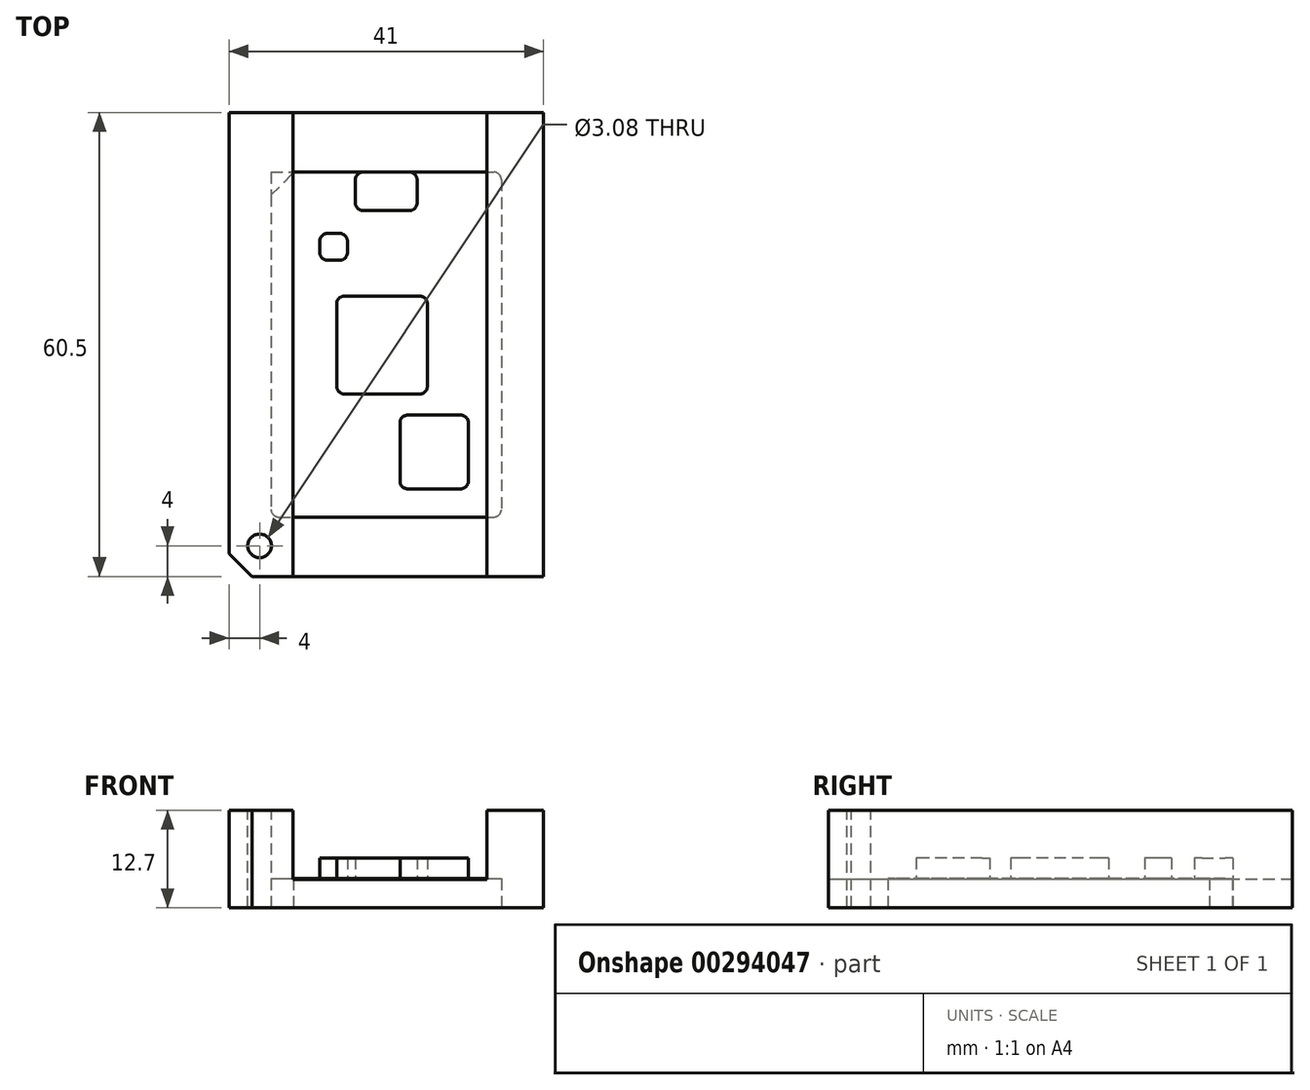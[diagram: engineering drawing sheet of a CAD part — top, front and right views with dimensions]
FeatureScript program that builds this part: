
annotation { "Feature Type Name" : "Feature", "Feature Type Description" : "" }
export const myFeature = defineFeature(function(context is Context, id is Id, definition is map)
    precondition{}
    {
        {
            var Q0;
            Q0=qCreatedBy(makeId("Top.planeOp"),FACE);
            var sketch = newSketch(context, id + "F0", { "sketchPlane" : qUnion([Q0])});
            skLineSegment(sketch, "E0.bottom", {"start": v(-20.5, -30.25) * mm, "end": v(20.5, -30.25) * mm});
            skLineSegment(sketch, "E0.top", {"start": v(-20.5, 30.25) * mm, "end": v(20.5, 30.25) * mm});
            skLineSegment(sketch, "E0.left", {"start": v(-20.5, -30.25) * mm, "end": v(-20.5, 30.25) * mm});
            skLineSegment(sketch, "E0.right", {"start": v(20.5, -30.25) * mm, "end": v(20.5, 30.25) * mm});
            skPoint(sketch, "E0.middle", {"position": v(0, 0) * mm});
            skSolve(sketch);
        }
        {
            var Q0;
            Q0 = qSketchRegion(id + "F0", true);
            extrude(context, id + "F1", {"entities" : qUnion([Q0]), "depth" : 12.7 * mm});
        }
        {
            var Q0;
            Q0=makeQuery(id+"F1.opExtrude","CAP_FACE",FACE,{"disambiguationData":[OSD([sQuery(id+"F0.wireOp",EDGE,"E0.bottom"),sQuery(id+"F0.wireOp",EDGE,"E0.top"),sQuery(id+"F0.wireOp",EDGE,"E0.left"),sQuery(id+"F0.wireOp",EDGE,"E0.right")])],"isStart":false});
            var sketch = newSketch(context, id + "F2", { "sketchPlane" : qUnion([Q0])});
            skLineSegment(sketch, "E1", {"start": v(-20.5, -27.25) * mm, "end": v(-17.5, -30.25) * mm});
            skLineSegment(sketch, "E2", {"start": v(-17.5, -30.25) * mm, "end": v(-20.5, -30.25) * mm});
            skLineSegment(sketch, "E3", {"start": v(-20.5, -30.25) * mm, "end": v(-20.5, -27.25) * mm});
            skCircle(sketch, "E4", {"center": v(-16.5, -26.25) * mm, "radius": 1.54 * mm});
            skLineSegment(sketch, "E5", {"start": v(-20.5, -30.25) * mm, "end": v(-20.5, -26.25) * mm, "construction": true});
            skLineSegment(sketch, "E6", {"start": v(-20.5, -26.25) * mm, "end": v(-16.5, -26.25) * mm, "construction": true});
            skSolve(sketch);
        }
        {
            var Q0;
            Q0 = qSketchRegion(id + "F2", true);
            extrude(context, id + "F3", {"entities" : qUnion([Q0]), "operationType" : NewBodyOperationType.REMOVE, "oppositeDirection" : true, "depth" : 25 * mm});
        }
        {
            var Q0;
            Q0=makeQuery(id+"F1.opExtrude","CAP_FACE",FACE,{"disambiguationData":[OSD([sQuery(id+"F0.wireOp",EDGE,"E0.bottom"),sQuery(id+"F0.wireOp",EDGE,"E0.top"),sQuery(id+"F0.wireOp",EDGE,"E0.left"),sQuery(id+"F0.wireOp",EDGE,"E0.right")])],"isStart":false});
            var sketch = newSketch(context, id + "F4", { "sketchPlane" : qUnion([Q0])});
            skLineSegment(sketch, "E7.bottom", {"start": v(-12.13, 30.25) * mm, "end": v(13.1, 30.25) * mm});
            skLineSegment(sketch, "E7.top", {"start": v(-12.13, -30.25) * mm, "end": v(13.1, -30.25) * mm});
            skLineSegment(sketch, "E7.left", {"start": v(-12.13, 30.25) * mm, "end": v(-12.13, -30.25) * mm});
            skLineSegment(sketch, "E7.right", {"start": v(13.1, 30.25) * mm, "end": v(13.1, -30.25) * mm});
            skSolve(sketch);
        }
        {
            var Q0;
            Q0 = qSketchRegion(id + "F4", true);
            extrude(context, id + "F5", {"entities" : qUnion([Q0]), "operationType" : NewBodyOperationType.REMOVE, "oppositeDirection" : true, "depth" : 9 * mm});
        }
        {
            var Q0;
            Q0=qCreatedBy(makeId("Top.planeOp"),FACE);
            var sketch = newSketch(context, id + "F6", { "sketchPlane" : qUnion([Q0])});
            skLineSegment(sketch, "E8.bottom", {"start": v(-15, 22.5) * mm, "end": v(15, 22.5) * mm});
            skLineSegment(sketch, "E8.top", {"start": v(-15, -22.5) * mm, "end": v(15, -22.5) * mm});
            skLineSegment(sketch, "E8.left", {"start": v(-15, 22.5) * mm, "end": v(-15, -22.5) * mm});
            skLineSegment(sketch, "E8.right", {"start": v(15, 22.5) * mm, "end": v(15, -22.5) * mm});
            skPoint(sketch, "E8.middle", {"position": v(0, 0) * mm});
            skSolve(sketch);
        }
        {
            var Q0;
            Q0 = qSketchRegion(id + "F6", true);
            extrude(context, id + "F7", {"entities" : qUnion([Q0]), "depth" : 3.8 * mm});
        }
        {
            var Q0;
            Q0=makeQuery(id+"F7.opExtrude","CAP_FACE",FACE,{"disambiguationData":[OSD([sQuery(id+"F6.wireOp",EDGE,"E8.bottom"),sQuery(id+"F6.wireOp",EDGE,"E8.top"),sQuery(id+"F6.wireOp",EDGE,"E8.left"),sQuery(id+"F6.wireOp",EDGE,"E8.right")])],"isStart":false});
            var sketch = newSketch(context, id + "F8", { "sketchPlane" : qUnion([Q0])});
            skLineSegment(sketch, "E9.bottom", {"start": v(-6.45, 6.32) * mm, "end": v(5.36, 6.32) * mm});
            skLineSegment(sketch, "E9.top", {"start": v(-6.45, -6.45) * mm, "end": v(5.36, -6.45) * mm});
            skLineSegment(sketch, "E9.left", {"start": v(-6.45, 6.32) * mm, "end": v(-6.45, -6.45) * mm});
            skLineSegment(sketch, "E9.right", {"start": v(5.36, 6.32) * mm, "end": v(5.36, -6.45) * mm});
            skLineSegment(sketch, "E10.bottom", {"start": v(1.79, -9.2) * mm, "end": v(10.71, -9.2) * mm});
            skLineSegment(sketch, "E10.top", {"start": v(1.79, -18.81) * mm, "end": v(10.71, -18.81) * mm});
            skLineSegment(sketch, "E10.left", {"start": v(1.79, -9.2) * mm, "end": v(1.79, -18.81) * mm});
            skLineSegment(sketch, "E10.right", {"start": v(10.71, -9.2) * mm, "end": v(10.71, -18.81) * mm});
            skLineSegment(sketch, "E11.bottom", {"start": v(-4.02, 17.47) * mm, "end": v(4.02, 17.47) * mm});
            skLineSegment(sketch, "E11.top", {"start": v(-4.02, 22.5) * mm, "end": v(4.02, 22.5) * mm});
            skLineSegment(sketch, "E11.left", {"start": v(-4.02, 17.47) * mm, "end": v(-4.02, 22.5) * mm});
            skLineSegment(sketch, "E11.right", {"start": v(4.02, 17.47) * mm, "end": v(4.02, 22.5) * mm});
            skLineSegment(sketch, "E12.bottom", {"start": v(-8.65, 14.5) * mm, "end": v(-5.07, 14.5) * mm});
            skLineSegment(sketch, "E12.top", {"start": v(-8.65, 10.99) * mm, "end": v(-5.07, 10.99) * mm});
            skLineSegment(sketch, "E12.left", {"start": v(-8.65, 14.5) * mm, "end": v(-8.65, 10.99) * mm});
            skLineSegment(sketch, "E12.right", {"start": v(-5.07, 14.5) * mm, "end": v(-5.07, 10.99) * mm});
            skLineSegment(sketch, "E13", {"start": v(0, 17.47) * mm, "end": v(0, -22.5) * mm, "construction": true});
            skSolve(sketch);
        }
        {
            var Q0;
            Q0 = qSketchRegion(id + "F8", true);
            extrude(context, id + "F9", {"entities" : qUnion([Q0]), "operationType" : NewBodyOperationType.ADD, "depth" : 2.7 * mm});
        }
        {
            var Q0;
            Q0=makeQuery(id+"F7.opExtrude","CAP_FACE",FACE,{"disambiguationData":[OSD([sQuery(id+"F6.wireOp",EDGE,"E8.bottom"),sQuery(id+"F6.wireOp",EDGE,"E8.top"),sQuery(id+"F6.wireOp",EDGE,"E8.left"),sQuery(id+"F6.wireOp",EDGE,"E8.right")])],"isStart":false});
            var sketch = newSketch(context, id + "F10", { "sketchPlane" : qUnion([Q0])});
            skLineSegment(sketch, "E14", {"start": v(-15, 19.5) * mm, "end": v(-12, 22.5) * mm});
            skLineSegment(sketch, "E15", {"start": v(-12, 22.5) * mm, "end": v(-15, 22.5) * mm});
            skLineSegment(sketch, "E16", {"start": v(-15, 19.5) * mm, "end": v(-15, 22.5) * mm});
            skSolve(sketch);
        }
        {
            var Q0;
            Q0 = qSketchRegion(id + "F10", true);
            extrude(context, id + "F11", {"entities" : qUnion([Q0]), "operationType" : NewBodyOperationType.REMOVE, "oppositeDirection" : true, "depth" : 25 * mm});
        }
        {
            var Q0;
            Q0=makeQuery(id+"F7.opExtrude","SWEPT_EDGE",EDGE,{"disambiguationData":[OSD([sQuery(id+"F6.wireOp",EDGE,"E8.bottom"),sQuery(id+"F6.wireOp",EDGE,"E8.right")])]});
            var Q1;
            Q1=makeQuery(id+"F7.opExtrude","SWEPT_EDGE",EDGE,{"disambiguationData":[OSD([sQuery(id+"F6.wireOp",EDGE,"E8.top"),sQuery(id+"F6.wireOp",EDGE,"E8.right")])]});
            var Q2;
            Q2=makeQuery(id+"F7.opExtrude","SWEPT_EDGE",EDGE,{"disambiguationData":[OSD([sQuery(id+"F6.wireOp",EDGE,"E8.top"),sQuery(id+"F6.wireOp",EDGE,"E8.left")])]});
            var Q3;
            Q3=makeQuery(id+"F11.boolean.opBoolean","COPY",EDGE,{"derivedFrom":makeQuery(id+"F11.opExtrude","SWEPT_EDGE",EDGE,{"disambiguationData":[OSD([sQuery(id+"F6.wireOp",EDGE,"E8.left"),sQuery(id+"F10.wireOp",EDGE,"E14"),sQuery(id+"F10.wireOp",EDGE,"E16")])]})});
            var Q4;
            Q4=makeQuery(id+"F11.boolean.opBoolean","COPY",EDGE,{"derivedFrom":makeQuery(id+"F11.opExtrude","SWEPT_EDGE",EDGE,{"disambiguationData":[OSD([sQuery(id+"F6.wireOp",EDGE,"E8.bottom"),sQuery(id+"F10.wireOp",EDGE,"E14"),sQuery(id+"F10.wireOp",EDGE,"E15")])]})});
            fillet(context, id + "F12", {"entities" : qUnion([Q0, Q1, Q2, Q3, Q4]), "radius" : 1 * mm, "tangentPropagation" : true, "allowEdgeOverflow" : false});
        }
        {
            var Q0;
            Q0=makeQuery(id+"F9.opExtrude","SWEPT_EDGE",EDGE,{"disambiguationData":[OSD([sQuery(id+"F8.wireOp",EDGE,"E9.top"),sQuery(id+"F8.wireOp",EDGE,"E9.right")])]});
            var Q1;
            Q1=makeQuery(id+"F9.opExtrude","SWEPT_EDGE",EDGE,{"disambiguationData":[OSD([sQuery(id+"F8.wireOp",EDGE,"E9.top"),sQuery(id+"F8.wireOp",EDGE,"E9.left")])]});
            var Q2;
            Q2=makeQuery(id+"F9.opExtrude","SWEPT_EDGE",EDGE,{"disambiguationData":[OSD([sQuery(id+"F8.wireOp",EDGE,"E10.top"),sQuery(id+"F8.wireOp",EDGE,"E10.left")])]});
            var Q3;
            Q3=makeQuery(id+"F9.opExtrude","SWEPT_EDGE",EDGE,{"disambiguationData":[OSD([sQuery(id+"F8.wireOp",EDGE,"E10.top"),sQuery(id+"F8.wireOp",EDGE,"E10.right")])]});
            var Q4;
            Q4=makeQuery(id+"F9.opExtrude","SWEPT_EDGE",EDGE,{"disambiguationData":[OSD([sQuery(id+"F8.wireOp",EDGE,"E9.bottom"),sQuery(id+"F8.wireOp",EDGE,"E9.right")])]});
            var Q5;
            Q5=makeQuery(id+"F9.opExtrude","SWEPT_EDGE",EDGE,{"disambiguationData":[OSD([sQuery(id+"F8.wireOp",EDGE,"E12.top"),sQuery(id+"F8.wireOp",EDGE,"E12.left")])]});
            var Q6;
            Q6=makeQuery(id+"F9.opExtrude","SWEPT_EDGE",EDGE,{"disambiguationData":[OSD([sQuery(id+"F8.wireOp",EDGE,"E12.top"),sQuery(id+"F8.wireOp",EDGE,"E12.right")])]});
            var Q7;
            Q7=makeQuery(id+"F9.opExtrude","SWEPT_EDGE",EDGE,{"disambiguationData":[OSD([sQuery(id+"F8.wireOp",EDGE,"E12.bottom"),sQuery(id+"F8.wireOp",EDGE,"E12.right")])]});
            var Q8;
            Q8=makeQuery(id+"F9.opExtrude","SWEPT_EDGE",EDGE,{"disambiguationData":[OSD([sQuery(id+"F8.wireOp",EDGE,"E11.bottom"),sQuery(id+"F8.wireOp",EDGE,"E11.left")])]});
            var Q9;
            Q9=makeQuery(id+"F9.opExtrude","SWEPT_EDGE",EDGE,{"disambiguationData":[OSD([sQuery(id+"F8.wireOp",EDGE,"E11.bottom"),sQuery(id+"F8.wireOp",EDGE,"E11.right")])]});
            var Q10;
            Q10=makeQuery(id+"F9.opExtrude","SWEPT_EDGE",EDGE,{"disambiguationData":[OSD([sQuery(id+"F6.wireOp",EDGE,"E8.bottom"),sQuery(id+"F8.wireOp",EDGE,"E11.top"),sQuery(id+"F8.wireOp",EDGE,"E11.right")])]});
            var Q11;
            Q11=makeQuery(id+"F9.opExtrude","SWEPT_EDGE",EDGE,{"disambiguationData":[OSD([sQuery(id+"F8.wireOp",EDGE,"E9.bottom"),sQuery(id+"F8.wireOp",EDGE,"E9.left")])]});
            var Q12;
            Q12=makeQuery(id+"F9.opExtrude","SWEPT_EDGE",EDGE,{"disambiguationData":[OSD([sQuery(id+"F8.wireOp",EDGE,"E12.bottom"),sQuery(id+"F8.wireOp",EDGE,"E12.left")])]});
            var Q13;
            Q13=makeQuery(id+"F9.opExtrude","SWEPT_EDGE",EDGE,{"disambiguationData":[OSD([sQuery(id+"F8.wireOp",EDGE,"E10.bottom"),sQuery(id+"F8.wireOp",EDGE,"E10.left")])]});
            var Q14;
            Q14=makeQuery(id+"F9.opExtrude","SWEPT_EDGE",EDGE,{"disambiguationData":[OSD([sQuery(id+"F6.wireOp",EDGE,"E8.bottom"),sQuery(id+"F8.wireOp",EDGE,"E11.top"),sQuery(id+"F8.wireOp",EDGE,"E11.left")])]});
            var Q15;
            Q15=makeQuery(id+"F9.opExtrude","SWEPT_EDGE",EDGE,{"disambiguationData":[OSD([sQuery(id+"F8.wireOp",EDGE,"E10.bottom"),sQuery(id+"F8.wireOp",EDGE,"E10.right")])]});
            fillet(context, id + "F13", {"entities" : qUnion([Q0, Q1, Q2, Q3, Q4, Q5, Q6, Q7, Q8, Q9, Q10, Q11, Q12, Q13, Q14, Q15]), "radius" : 1 * mm, "tangentPropagation" : true, "allowEdgeOverflow" : false});
        }
    });
